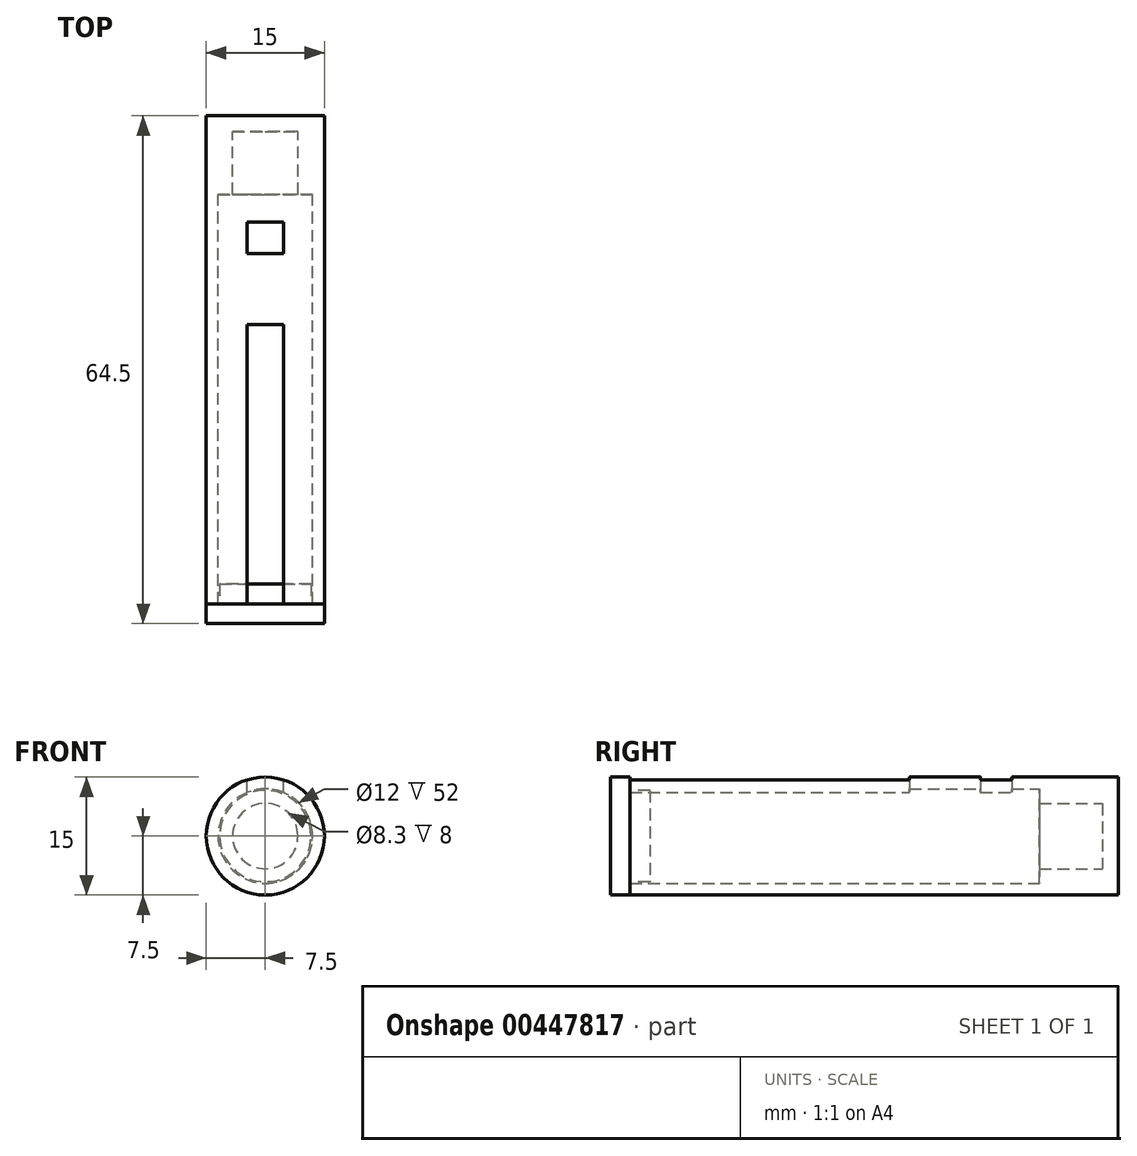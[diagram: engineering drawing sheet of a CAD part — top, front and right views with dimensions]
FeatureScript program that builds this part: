
annotation { "Feature Type Name" : "Feature", "Feature Type Description" : "" }
export const myFeature = defineFeature(function(context is Context, id is Id, definition is map)
    precondition{}
    {
        {
            var Q0;
            Q0=qCreatedBy(makeId("Front.planeOp"),FACE);
            var sketch = newSketch(context, id + "F0", { "sketchPlane" : qUnion([Q0])});
            skCircle(sketch, "E0", {"center": v(0, 0) * mm, "radius": 6 * mm});
            skCircle(sketch, "E1.0", {"center": v(0, 0) * mm, "radius": 7.5 * mm});
            skSolve(sketch);
        }
        {
            var Q0;
            Q0 = qSketchRegion(id + "F0", true);
            extrude(context, id + "F1", {"entities" : qUnion([Q0]), "depth" : 60 * mm});
        }
        {
            var Q0;
            Q0=makeQuery(id+"F1.opExtrude","CAP_FACE",FACE,{"disambiguationData":[OSD([sQuery(id+"F0.wireOp",EDGE,"E0"),sQuery(id+"F0.wireOp",EDGE,"E1.0")])],"isStart":true});
            var sketch = newSketch(context, id + "F2", { "sketchPlane" : qUnion([Q0])});
            skCircle(sketch, "E2.0", {"center": v(0, 0) * mm, "radius": 6 * mm});
            skCircle(sketch, "E3", {"center": v(0, 0) * mm, "radius": 4.15 * mm});
            skSolve(sketch);
        }
        {
            var Q0;
            Q0 = qSketchRegion(id + "F2", true);
            extrude(context, id + "F3", {"entities" : qUnion([Q0]), "operationType" : NewBodyOperationType.ADD, "oppositeDirection" : true, "depth" : 8 * mm});
        }
        {
            var Q0;
            Q0=makeQuery(id+"F3.boolean.opBoolean","MERGE",FACE,{"derivedFrom":[makeQuery(id+"F1.opExtrude","CAP_FACE",FACE,{"disambiguationData":[OSD([sQuery(id+"F0.wireOp",EDGE,"E0"),sQuery(id+"F0.wireOp",EDGE,"E1.0")])],"isStart":true}),makeQuery(id+"F3.opExtrude","CAP_FACE",FACE,{"disambiguationData":[OSD([sQuery(id+"F2.wireOp",EDGE,"E2.0"),sQuery(id+"F2.wireOp",EDGE,"E3")])],"isStart":true})]});
            var sketch = newSketch(context, id + "F4", { "sketchPlane" : qUnion([Q0])});
            skCircle(sketch, "E4.0", {"center": v(0, 0) * mm, "radius": 7.5 * mm});
            skSolve(sketch);
        }
        {
            var Q0;
            Q0 = qSketchRegion(id + "F4", true);
            extrude(context, id + "F5", {"entities" : qUnion([Q0]), "operationType" : NewBodyOperationType.ADD, "depth" : 2 * mm});
        }
        {
            var Q0;
            Q0=qCreatedBy(makeId("Top.planeOp"),FACE);
            var sketch = newSketch(context, id + "F6", { "sketchPlane" : qUnion([Q0])});
            skLineSegment(sketch, "E5.bottom", {"start": v(-2.3, -24.5) * mm, "end": v(2.3, -24.5) * mm});
            skLineSegment(sketch, "E5.top", {"start": v(-2.3, -90) * mm, "end": v(2.3, -90) * mm});
            skLineSegment(sketch, "E5.left", {"start": v(-2.3, -24.5) * mm, "end": v(-2.3, -90) * mm});
            skLineSegment(sketch, "E5.right", {"start": v(2.3, -24.5) * mm, "end": v(2.3, -90) * mm});
            skLineSegment(sketch, "E6", {"start": v(0, -24.5) * mm, "end": v(0, 0) * mm, "construction": true});
            skLineSegment(sketch, "E7.bottom", {"start": v(-2.3, -15.5) * mm, "end": v(2.3, -15.5) * mm});
            skLineSegment(sketch, "E7.top", {"start": v(-2.3, -11.5) * mm, "end": v(2.3, -11.5) * mm});
            skLineSegment(sketch, "E7.left", {"start": v(-2.3, -15.5) * mm, "end": v(-2.3, -11.5) * mm});
            skLineSegment(sketch, "E7.right", {"start": v(2.3, -15.5) * mm, "end": v(2.3, -11.5) * mm});
            skSolve(sketch);
        }
        {
            var Q0;
            Q0 = qSketchRegion(id + "F6", true);
            extrude(context, id + "F7", {"entities" : qUnion([Q0]), "operationType" : NewBodyOperationType.REMOVE, "depth" : 25 * mm});
        }
        {
            var Q0;
            Q0=makeQuery(id+"F1.opExtrude","CAP_FACE",FACE,{"disambiguationData":[OSD([sQuery(id+"F0.wireOp",EDGE,"E0"),sQuery(id+"F0.wireOp",EDGE,"E1.0")])],"isStart":false});
            var sketch = newSketch(context, id + "F8", { "sketchPlane" : qUnion([Q0])});
            skCircle(sketch, "E8", {"center": v(0, 0) * mm, "radius": 7.5 * mm});
            skSolve(sketch);
        }
        {
            var Q0;
            Q0 = qSketchRegion(id + "F8", true);
            extrude(context, id + "F9", {"entities" : qUnion([Q0]), "depth" : 2.5 * mm});
        }
        {
            var Q0;
            Q0=makeQuery(id+"F9.opExtrude","CAP_FACE",FACE,{"disambiguationData":[OSD([sQuery(id+"F8.wireOp",EDGE,"E8")])],"isStart":true});
            var sketch = newSketch(context, id + "F10", { "sketchPlane" : qUnion([Q0])});
            skCircle(sketch, "E9", {"center": v(0, 0) * mm, "radius": 5.8 * mm});
            skSolve(sketch);
        }
        {
            var Q0;
            Q0 = qSketchRegion(id + "F10", true);
            extrude(context, id + "F11", {"entities" : qUnion([Q0]), "operationType" : NewBodyOperationType.ADD, "depth" : 2.5 * mm});
        }
    });
